# Revit family: 820-10-028-DN200-300
name_source: partatom
category: Pipe Accessories
units: mm (PartAtom-declared; Revit-internal decimal feet)

## family parameters
Always vertical = Yes
Cut with Voids When Loaded = No
Part Type = Valve - Breaks Into
Round Connector Dimension = Use Diameter
Shared = No
Work Plane-Based = No

## types (6) — shared parameters
3 = 3 mm  [stored 0.00984252 ft]
Body_wallthickness = 10 mm  [stored 0.0328084 ft]
DN200_PN10 = 820-0200-10-521L0030002
DN200_PN16 = 820-0200-10-521L0160002
DN250_PN10 = 820-0250-10-521L0030002
DN250_PN16 = 820-0250-10-521L0160002
DN300_PN10 = 820-0300-10-521L0030002
DN300_PN16 = 820-0300-10-521L0160002
Description_ = AVK CENTRIC LUG BUTTERFLY VALVE, PN10/16
Flange_thickness = 10 mm  [stored 0.0328084 ft]
Search_table = 820-10-028-DN200-300
URL product pages = https://www.avkvalves.com
fillet = 20 mm  [stored 0.0656168 ft]
zero-valued in all types: Default Elevation

## per-type parameters (varying)
| type | Actuator_Dia | Bore | Cut | DN | EPDM | F | F2 | H2 | Hole_dia | ID | L | L2 | LUG_T | L_ref | L_ref_2 | L_ref_3 | Lug_D | Lug_D1 | PCD | Rubber_ID | Rubber_r | W2_ref | disk |
| DN200_PN10 | 90 mm  [stored 0.295276 ft] | 100 mm  [stored 0.328084 ft] | 198 mm | 200 mm | 99 mm  [stored 0.324803 ft] | 17 mm  [stored 0.0557743 ft] | 19 mm  [stored 0.062336 ft] | 161 mm  [stored 0.528215 ft] | 31 mm  [stored 0.101706 ft] | 100 mm  [stored 0.328084 ft] | 60 mm  [stored 0.19685 ft] | 166 mm  [stored 0.544619 ft] | 24 mm  [stored 0.0787402 ft] | 40 mm  [stored 0.131234 ft] | 80 mm  [stored 0.262467 ft] | 33 mm  [stored 0.108268 ft] | 20 mm  [stored 0.0656168 ft] | 35 mm  [stored 0.114829 ft] | 160 mm  [stored 0.524934 ft] | 98 mm  [stored 0.321522 ft] | 105 mm  [stored 0.344488 ft] | 240 mm | 17 mm  [stored 0.0557743 ft] |
| DN200_PN16 | 90 mm  [stored 0.295276 ft] | 100 mm  [stored 0.328084 ft] | 198 mm | 200 mm | 99 mm  [stored 0.324803 ft] | 17 mm  [stored 0.0557743 ft] | 19 mm  [stored 0.062336 ft] | 161 mm  [stored 0.528215 ft] | 31 mm  [stored 0.101706 ft] | 100 mm  [stored 0.328084 ft] | 60 mm  [stored 0.19685 ft] | 166 mm  [stored 0.544619 ft] | 24 mm  [stored 0.0787402 ft] | 40 mm  [stored 0.131234 ft] | 80 mm  [stored 0.262467 ft] | 33 mm  [stored 0.108268 ft] | 20 mm  [stored 0.0656168 ft] | 35 mm  [stored 0.114829 ft] | 160 mm  [stored 0.524934 ft] | 98 mm  [stored 0.321522 ft] | 105 mm  [stored 0.344488 ft] | 240 mm | 17 mm  [stored 0.0557743 ft] |
| DN250_PN10 | 150 mm  [stored 0.492126 ft] | 125 mm  [stored 0.410105 ft] | 248 mm | 250 mm | 124 mm  [stored 0.406824 ft] | 22 mm  [stored 0.0721785 ft] | 24 mm  [stored 0.0787402 ft] | 199 mm | 34 mm  [stored 0.111549 ft] | 125 mm  [stored 0.410105 ft] | 68 mm  [stored 0.223097 ft] | 201 mm | 27 mm | 48 mm  [stored 0.15748 ft] | 96 mm  [stored 0.314961 ft] | 40 mm  [stored 0.131234 ft] | 22 mm  [stored 0.0721785 ft] | 39 mm  [stored 0.127953 ft] | 193 mm | 123 mm  [stored 0.403543 ft] | 130 mm  [stored 0.426509 ft] | 279 mm | 19 mm  [stored 0.062336 ft] |
| DN250_PN16 | 150 mm  [stored 0.492126 ft] | 125 mm  [stored 0.410105 ft] | 248 mm | 250 mm | 124 mm  [stored 0.406824 ft] | 22 mm  [stored 0.0721785 ft] | 24 mm  [stored 0.0787402 ft] | 199 mm | 34 mm  [stored 0.111549 ft] | 125 mm  [stored 0.410105 ft] | 68 mm  [stored 0.223097 ft] | 201 mm | 27 mm | 48 mm  [stored 0.15748 ft] | 96 mm  [stored 0.314961 ft] | 40 mm  [stored 0.131234 ft] | 22 mm  [stored 0.0721785 ft] | 39 mm  [stored 0.127953 ft] | 193 mm | 123 mm  [stored 0.403543 ft] | 130 mm  [stored 0.426509 ft] | 279 mm | 19 mm  [stored 0.062336 ft] |
| DN300_PN10 | 150 mm  [stored 0.492126 ft] | 150 mm  [stored 0.492126 ft] | 298 mm | 300 mm | 149 mm  [stored 0.488845 ft] | 22 mm  [stored 0.0721785 ft] | 24 mm  [stored 0.0787402 ft] | 234 mm | 34 mm  [stored 0.111549 ft] | 150 mm  [stored 0.492126 ft] | 78 mm  [stored 0.255906 ft] | 236 mm | 31 mm  [stored 0.101706 ft] | 58 mm  [stored 0.190289 ft] | 116 mm  [stored 0.380577 ft] | 48 mm  [stored 0.15748 ft] | 23 mm  [stored 0.0754593 ft] | 40 mm  [stored 0.131234 ft] | 225 mm | 148 mm  [stored 0.485564 ft] | 155 mm  [stored 0.50853 ft] | 315 mm | 22 mm  [stored 0.0721785 ft] |
| DN300_PN16 | 150 mm  [stored 0.492126 ft] | 150 mm  [stored 0.492126 ft] | 298 mm | 300 mm | 149 mm  [stored 0.488845 ft] | 22 mm  [stored 0.0721785 ft] | 24 mm  [stored 0.0787402 ft] | 234 mm | 34 mm  [stored 0.111549 ft] | 150 mm  [stored 0.492126 ft] | 78 mm  [stored 0.255906 ft] | 236 mm | 31 mm  [stored 0.101706 ft] | 58 mm  [stored 0.190289 ft] | 116 mm  [stored 0.380577 ft] | 48 mm  [stored 0.15748 ft] | 23 mm  [stored 0.0754593 ft] | 40 mm  [stored 0.131234 ft] | 225 mm | 148 mm  [stored 0.485564 ft] | 155 mm  [stored 0.50853 ft] | 315 mm | 22 mm  [stored 0.0721785 ft] |

note: [stored X ft] marks values corroborated as IEEE doubles in the binary element streams (Revit-internal decimal feet)

## geometry (parser evidence)
native form markers: Sweep x5
no freeform markers — native parametric forms only
